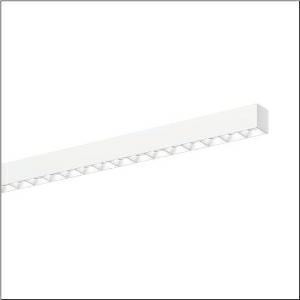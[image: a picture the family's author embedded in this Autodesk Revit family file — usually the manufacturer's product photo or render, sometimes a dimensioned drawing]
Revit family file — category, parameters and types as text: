
# Revit family: silica_r__21_51mx26dc4awb_5f84
name_source: partatom
category: Lighting Fixtures
units: mm (PartAtom-declared; Revit-internal decimal feet)

## family parameters
Cut with Voids When Loaded = No
Host = Face
Light Source = No
Part Type = Normal
Room Calculation Point = No
Round Connector Dimension = Use Diameter
Shared = No

## types (1)
- --- (1 x LED, 10800 lm, 60.6 W, 4000K)
    Apparent Load = 61 VA
    CIE Flux Codes = 83 98 100 100 100
    Color Rendering = 80
    Color Temperature = 4000K
    Default Elevation = 1800 mm
    Description = Silica® 21, office luminaire, primary light control with darklight reflector, of PMMA, white, CAT 2 (L<= 3000cd/m²), light emission: direct distribution, primary light characteristic: symmetric, installation type: surface-mounted, LED, rated luminous flux: 10.800lm, luminous efficacy: 178lm/W, light colour: 840, colour temperature: 4000K, control gear: DALI 2, with terminal, 3+2-pole, max. 2.5mm², mains connection: 220..240V, AC, 50/60Hz, rated input power: 60.6W, luminaire housing, of aluminium, traffic white (RAL 9016), length: 3.004mm, width: 53mm, height: 53mm, protection rating (complete): IP20, insulation class (complete): insulation class I (protective earthing), certification: CE, permissible operating ambient temperature: 0..+35°C, standard: EN 50419, packaging unit: 1 piece
    Height = 53 mm
    Lamp = 1 x LED
    Lamp Light Flux = 10800 lm
    Lamp Power = 60.6 W
    Lamp count = 1
    Length = 3004 mm
    Luminous efficacy = 178 lm/W
    Manufacturer = Siteco
    ModVariant = No
    Model = 51MX26DC4AWB
    Mounting Place = Ceiling
    Mounting Type = Surface mounted
    Number of Poles = 1
    OnlyDefault = Yes
    Power Factor = 1
    Product Name = Silica® 21
    Product group = office luminaire | ceiling mounted
    ProductGroupID = 301
    Protection Class = Protection class I
    Protection Degree = IP 20
    RLX_Detail_Level = 1
    RLX_Emergency_Light_Flux = 0 lm
    RLX_Emergency_Type = 0
    RLX_Emergency_Type_DB = No
    RlxData = <blob elided: 58657 chars, md5=4cc8cda4>
    Socket = socket
    Standby Power = 0 W
    System Light Flux = 10800 lm
    System Power = 61 W
    Type Comments = factory setting: luminous flux: 100 % | dim-lin: 254 | 336 mA
    Type Image = l_1335934.jpg
    URL = http://relux.com
    VarID = @adj_121606
    Voltage = 0 V
    Weight = 0.00 kg
    Width = 53 mm

## geometry (parser evidence)
native form markers: Blend x4, Sweep x11
no freeform markers — native parametric forms only
